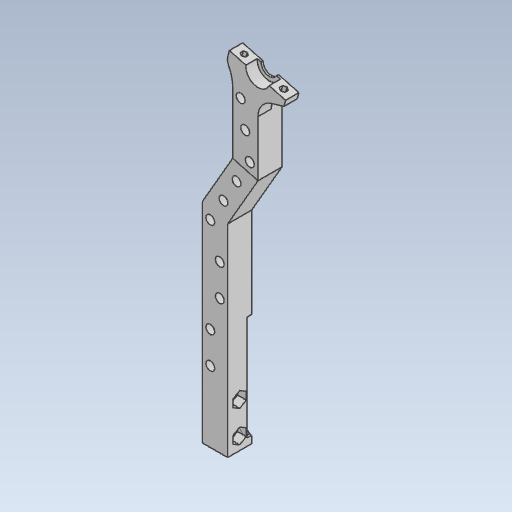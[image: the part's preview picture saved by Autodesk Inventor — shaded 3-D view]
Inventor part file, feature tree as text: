
AUTODESK INVENTOR PART (.ipt)
format: ipt  version: 2021.2 (Build 252289000, 289)  size: 311,808 bytes
history: native  units: mm
features: other x10, fillet x1, chamfer x1
ambient origin geometry x8: Origin, YZ Plane, XZ Plane, XY Plane, X Axis, Y Axis, Z Axis, Center Point
bodies: Body1 (feature_tree), Body2 (feature_tree)
feature tree (12):
  other  "Твёрдое тело.ipt"
  other  "РабПлоскость1"
  other  "Разделение1"
  fillet  "Сопряжение1"  Radius=10.0mm
  chamfer  "Фаска1"  Distance=2.0mm
  other  "Ножка 1::Твёрдое тело.ipt"
  other  "Элемент создания тегов1"
  other  "Твердое тело22::Твёрдое тело.ipt"
  other  "Твердое тело23::Твёрдое тело.ipt"
  other  "Твердое тело1"
  other  "Твердое тело2"
  other  "Твердое тело3"
